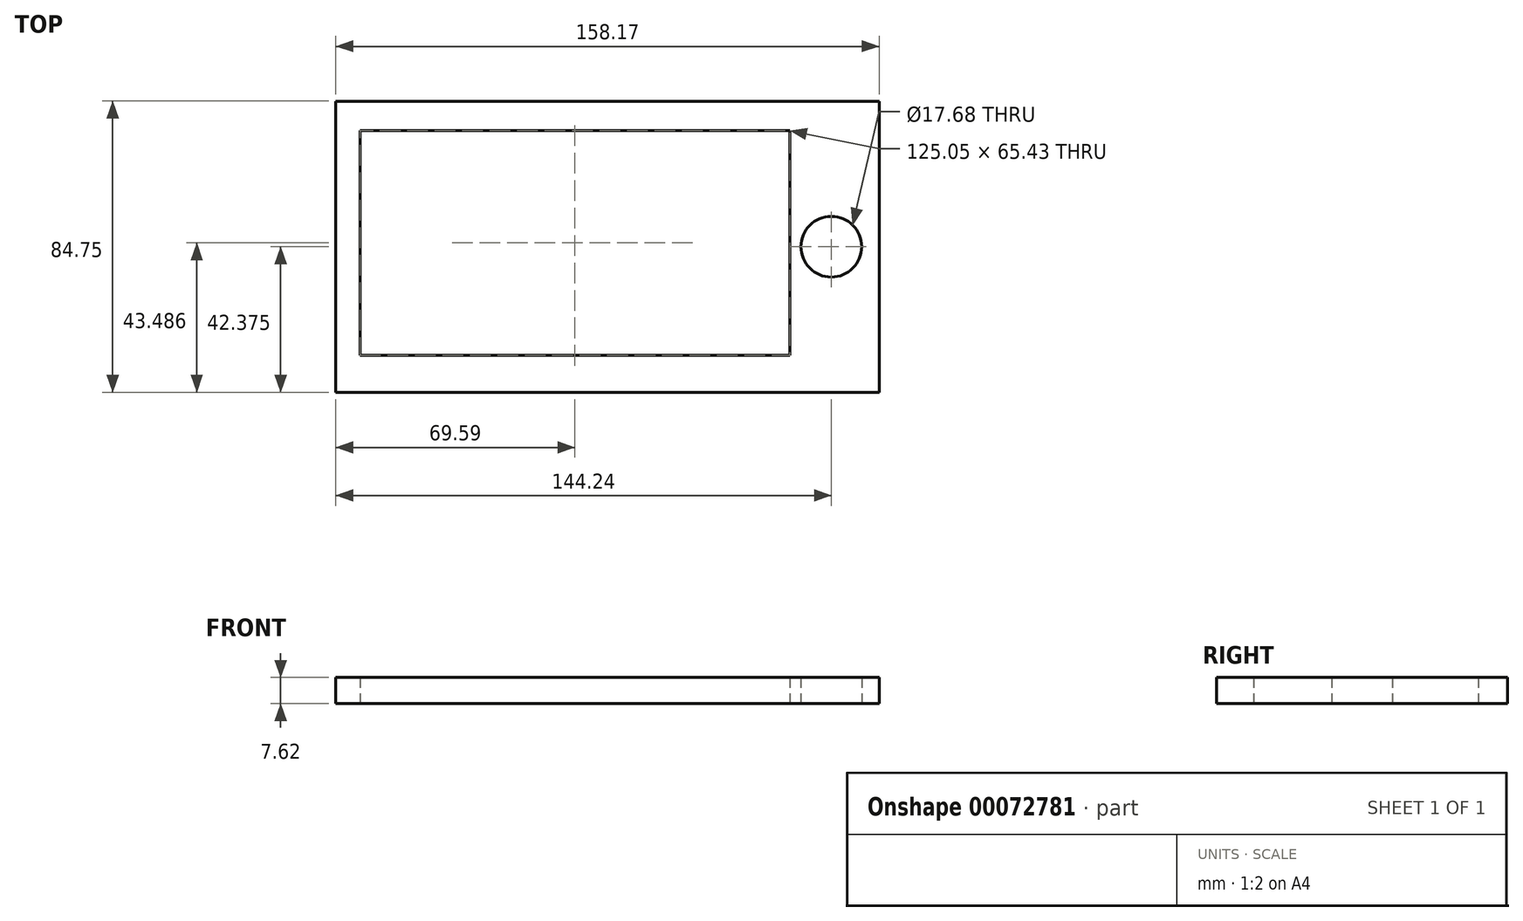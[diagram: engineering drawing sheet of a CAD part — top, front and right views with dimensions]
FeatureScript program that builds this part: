
annotation { "Feature Type Name" : "Feature", "Feature Type Description" : "" }
export const myFeature = defineFeature(function(context is Context, id is Id, definition is map)
    precondition{}
    {
        {
            var Q0;
            Q0=qCreatedBy(makeId("Top.planeOp"),FACE);
            var sketch = newSketch(context, id + "F0", { "sketchPlane" : qUnion([Q0])});
            skLineSegment(sketch, "E0.bottom", {"start": v(-86.85, 42.36) * mm, "end": v(71.32, 42.36) * mm});
            skLineSegment(sketch, "E0.top", {"start": v(-86.85, -42.39) * mm, "end": v(71.32, -42.39) * mm});
            skLineSegment(sketch, "E0.left", {"start": v(-86.85, 42.36) * mm, "end": v(-86.85, -42.39) * mm});
            skLineSegment(sketch, "E0.right", {"start": v(71.32, 42.36) * mm, "end": v(71.32, -42.39) * mm});
            skLineSegment(sketch, "E1.bottom", {"start": v(-79.79, 33.81) * mm, "end": v(45.26, 33.81) * mm});
            skLineSegment(sketch, "E1.top", {"start": v(-79.79, -31.62) * mm, "end": v(45.26, -31.62) * mm});
            skLineSegment(sketch, "E1.left", {"start": v(-79.79, 33.81) * mm, "end": v(-79.79, -31.62) * mm});
            skLineSegment(sketch, "E1.right", {"start": v(45.26, 33.81) * mm, "end": v(45.26, -31.62) * mm});
            skCircle(sketch, "E2", {"center": v(57.39, -0.02) * mm, "radius": 8.84 * mm});
            skPoint(sketch, "E2.centerSnap0", {"position": v(71.32, -0.02) * mm});
            skSolve(sketch);
        }
        {
            var Q0;
            Q0=makeQuery(id+"F0.imprint","IMPRINT",FACE,{"disambiguationData":[TD([[makeQuery(id+"F0.imprint","IMPRINT",EDGE,{"derivedFrom":sQuery(id+"F0.wireOp",EDGE,"E0.bottom")}),-1.0]])]});
            extrude(context, id + "F1", {"entities" : qUnion([Q0]), "depth" : 7.62 * mm});
        }
    });
